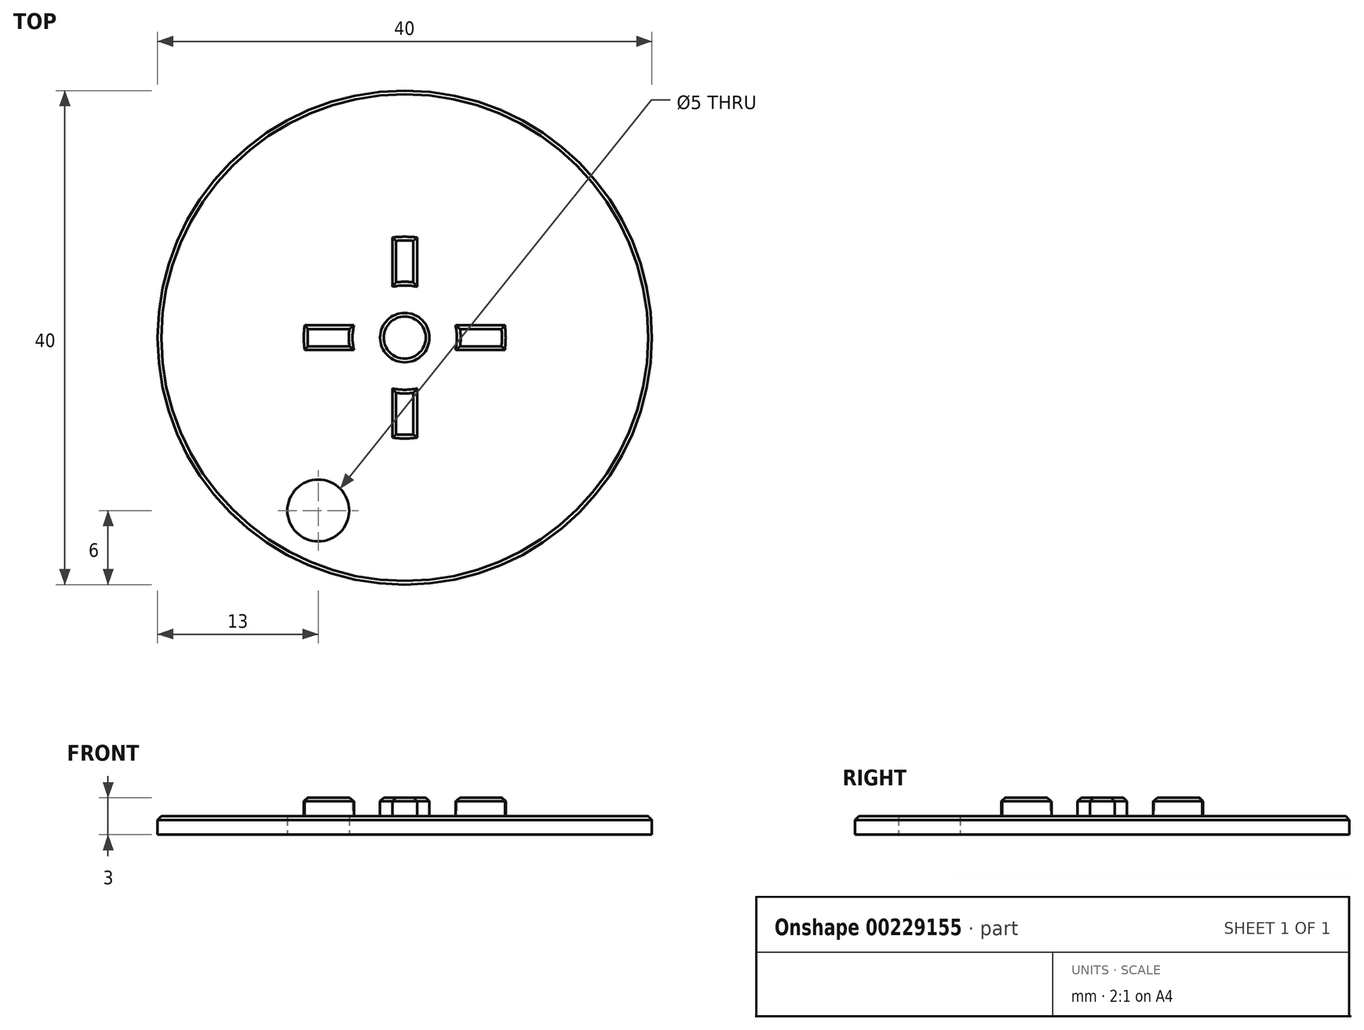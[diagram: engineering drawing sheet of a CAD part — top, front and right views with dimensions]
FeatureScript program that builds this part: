
annotation { "Feature Type Name" : "Feature", "Feature Type Description" : "" }
export const myFeature = defineFeature(function(context is Context, id is Id, definition is map)
    precondition{}
    {
        {
            var Q0;
            Q0=qCreatedBy(makeId("Top.planeOp"),FACE);
            var sketch = newSketch(context, id + "F0", { "sketchPlane" : qUnion([Q0])});
            skCircle(sketch, "E0", {"center": v(0, 0) * mm, "radius": 20 * mm});
            skLineSegment(sketch, "E1", {"start": v(-21.83, -14) * mm, "end": v(28.19, -14) * mm, "construction": true});
            skLineSegment(sketch, "E2", {"start": v(-7, 27.2) * mm, "end": v(-7, -24.35) * mm, "construction": true});
            skPoint(sketch, "E3", {"position": v(-7, -14) * mm});
            skSolve(sketch);
        }
        {
            var Q0;
            Q0=qSketchRegion(id+"F0",true);
            extrude(context, id + "F1", {"entities" : qUnion([Q0]), "depth" : 1.5 * mm});
        }
        {
            var Q0;
            Q0=sQuery(id+"F0.wireOp",VERTEX,"E3");
            var Q1;
            Q1=makeQuery(id+"F1.opExtrude","SWEPT_BODY",BODY,{"disambiguationData":[OSD([sQuery(id+"F0.wireOp",EDGE,"E0"),sQuery(id+"F0.wireOp",EDGE,"fWfHAkU1-x34K-Ojr9-oPNq-K8kwXMuBxkp4")])]});
            hole(context, id + "F2", {"style" : HoleStyle.SIMPLE, "endStyle" : HoleEndStyle.BLIND, "oppositeDirection" : true, "holeDiameter" : 5 * mm, "holeDepth" : 20.38 * mm, "tappedDepth" : 18 * mm, "tapClearance" : 3, "locations" : qUnion([Q0]), "scope" : qUnion([Q1])});
        }
        {
            var Q0;
            Q0=qCreatedBy(makeId("Top.planeOp"),FACE);
            var sketch = newSketch(context, id + "F3", { "sketchPlane" : qUnion([Q0])});
            skLineSegment(sketch, "E4", {"start": v(-21.03, -11.94) * mm, "end": v(28.98, -11.94) * mm, "construction": true});
            skLineSegment(sketch, "E5", {"start": v(-6.2, 28.77) * mm, "end": v(-6.2, -22.79) * mm, "construction": true});
            skPoint(sketch, "E6", {"position": v(-6.2, -11.94) * mm});
            skLineSegment(sketch, "E7", {"start": v(-8.1, 1) * mm, "end": v(-4.1, 1) * mm});
            skLineSegment(sketch, "E8", {"start": v(-1, 8.1) * mm, "end": v(-1, 4.1) * mm});
            skLineSegment(sketch, "E9", {"start": v(-10.06, 0) * mm, "end": v(9.04, 0) * mm, "construction": true});
            skLineSegment(sketch, "E10", {"start": v(0, 9.78) * mm, "end": v(0, -3.51) * mm, "construction": true});
            skLineSegment(sketch, "E11.MirrorCS", {"start": v(1, 8.1) * mm, "end": v(1, 4.1) * mm});
            skLineSegment(sketch, "E12.MirrorCS", {"start": v(-8.1, -1) * mm, "end": v(-4.1, -1) * mm});
            skLineSegment(sketch, "E13.MirrorCS", {"start": v(8.1, -1) * mm, "end": v(4.1, -1) * mm});
            skLineSegment(sketch, "E14.MirrorCS", {"start": v(8.1, 1) * mm, "end": v(4.1, 1) * mm});
            skLineSegment(sketch, "E15.MirrorCS", {"start": v(1, -8.1) * mm, "end": v(1, -4.1) * mm});
            skLineSegment(sketch, "E16.MirrorCS", {"start": v(-1, -8.1) * mm, "end": v(-1, -4.1) * mm});
            skArc(sketch, "E17", {"start": v(-1, -4.1) * mm, "mid": v(0, -4.23) * mm, "end": v(1, -4.1) * mm});
            skCircle(sketch, "E18", {"center": v(0, 0) * mm, "radius": 2 * mm});
            skArc(sketch, "E19.trimOffspring", {"start": v(4.1, -1) * mm, "mid": v(4.22, 0) * mm, "end": v(4.1, 1) * mm});
            skArc(sketch, "E20.trimOffspring", {"start": v(1, 4.1) * mm, "mid": v(0, 4.23) * mm, "end": v(-1, 4.1) * mm});
            skArc(sketch, "E21.trimOffspring", {"start": v(-4.1, 1) * mm, "mid": v(-4.22, 0) * mm, "end": v(-4.1, -1) * mm});
            skArc(sketch, "E22", {"start": v(8.1, -1) * mm, "mid": v(8.17, 0) * mm, "end": v(8.1, 1) * mm});
            skArc(sketch, "E23.trimOffspring", {"start": v(-1, -8.1) * mm, "mid": v(0, -8.17) * mm, "end": v(1, -8.1) * mm});
            skArc(sketch, "E24.trimOffspring", {"start": v(-8.1, 1) * mm, "mid": v(-8.17, 0) * mm, "end": v(-8.1, -1) * mm});
            skArc(sketch, "E25.trimOffspring", {"start": v(1, 8.1) * mm, "mid": v(0, 8.17) * mm, "end": v(-1, 8.1) * mm});
            skSolve(sketch);
        }
        {
            var Q0;
            Q0 = qSketchRegion(id + "F3", true);
            extrude(context, id + "F4", {"entities" : qUnion([Q0]), "operationType" : NewBodyOperationType.ADD, "depth" : 3 * mm});
        }
        {
            var Q0;
            Q0=makeQuery(id+"F4.opExtrude","CAP_FACE",FACE,{"disambiguationData":[OSD([sQuery(id+"F3.wireOp",EDGE,"E18")])],"isStart":false});
            var Q1;
            Q1=makeQuery(id+"F4.opExtrude","CAP_FACE",FACE,{"disambiguationData":[OSD([sQuery(id+"F3.wireOp",EDGE,"E8"),sQuery(id+"F3.wireOp",EDGE,"E11.MirrorCS"),sQuery(id+"F3.wireOp",EDGE,"E20.trimOffspring"),sQuery(id+"F3.wireOp",EDGE,"E25.trimOffspring")])],"isStart":false});
            var Q2;
            Q2=makeQuery(id+"F4.opExtrude","CAP_FACE",FACE,{"disambiguationData":[OSD([sQuery(id+"F3.wireOp",EDGE,"E13.MirrorCS"),sQuery(id+"F3.wireOp",EDGE,"E14.MirrorCS"),sQuery(id+"F3.wireOp",EDGE,"E19.trimOffspring"),sQuery(id+"F3.wireOp",EDGE,"E22")])],"isStart":false});
            var Q3;
            Q3=makeQuery(id+"F4.opExtrude","CAP_FACE",FACE,{"disambiguationData":[OSD([sQuery(id+"F3.wireOp",EDGE,"E15.MirrorCS"),sQuery(id+"F3.wireOp",EDGE,"E16.MirrorCS"),sQuery(id+"F3.wireOp",EDGE,"E17"),sQuery(id+"F3.wireOp",EDGE,"E23.trimOffspring")])],"isStart":false});
            var Q4;
            Q4=makeQuery(id+"F4.opExtrude","CAP_FACE",FACE,{"disambiguationData":[OSD([sQuery(id+"F3.wireOp",EDGE,"E7"),sQuery(id+"F3.wireOp",EDGE,"E12.MirrorCS"),sQuery(id+"F3.wireOp",EDGE,"E21.trimOffspring"),sQuery(id+"F3.wireOp",EDGE,"E24.trimOffspring")])],"isStart":false});
            var Q5;
            Q5=makeQuery(id+"F1.opExtrude","CAP_EDGE",EDGE,{"disambiguationData":[OSD([sQuery(id+"F0.wireOp",EDGE,"E0")])],"isStart":false});
            chamfer(context, id + "F5", {"entities" : qUnion([Q0, Q1, Q2, Q3, Q4, Q5]), "width" : .3 * mm, "tangentPropagation" : true});
        }
    });
